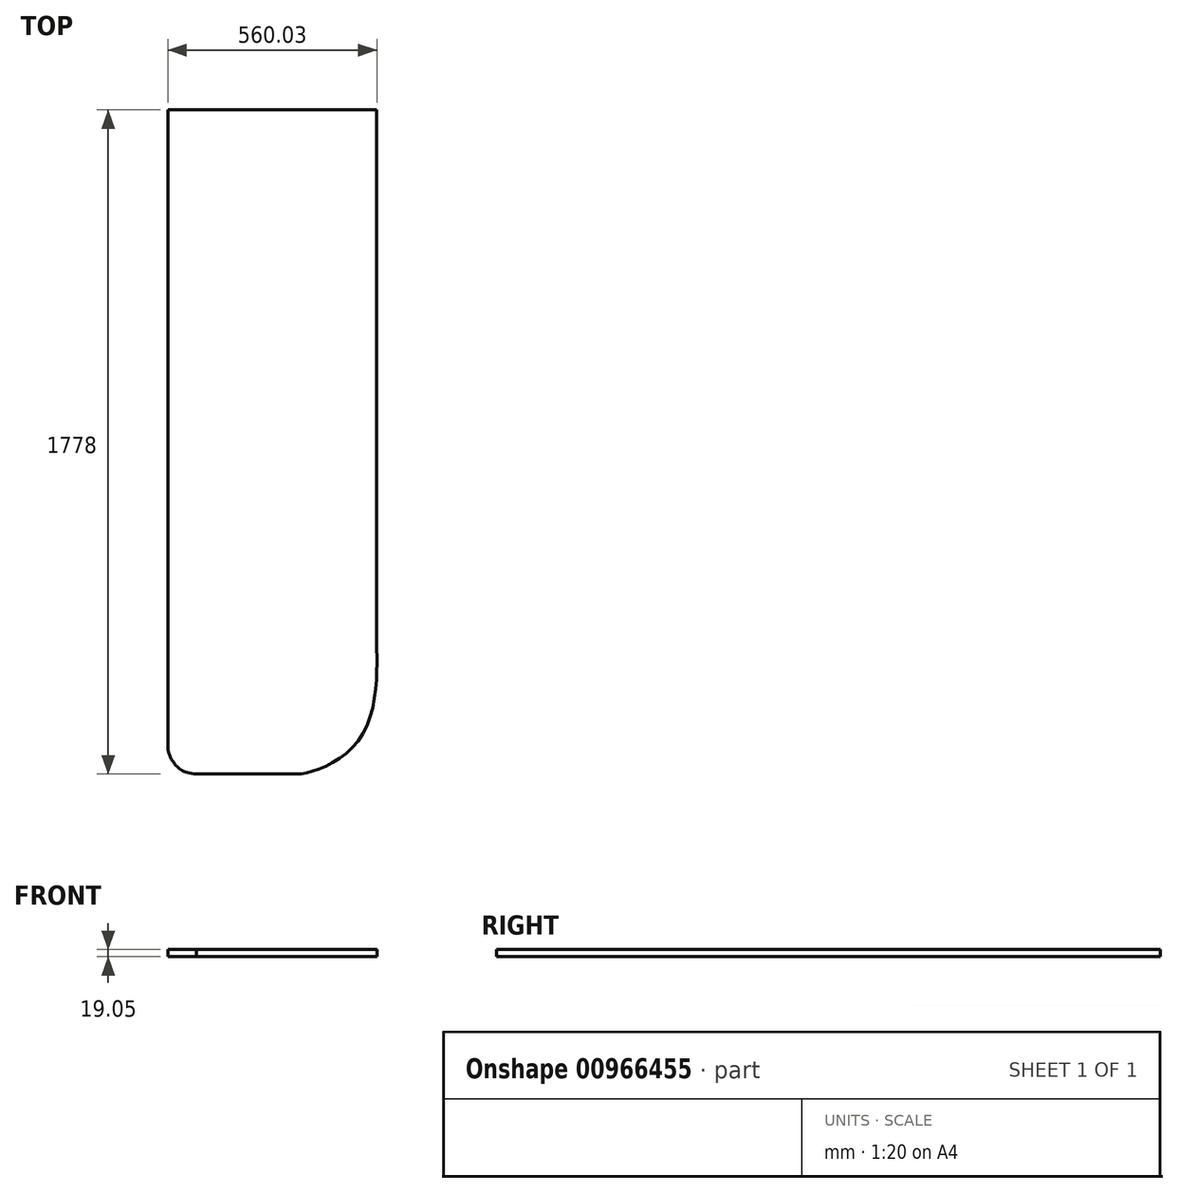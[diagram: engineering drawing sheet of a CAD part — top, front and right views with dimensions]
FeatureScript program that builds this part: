
annotation { "Feature Type Name" : "Feature", "Feature Type Description" : "" }
export const myFeature = defineFeature(function(context is Context, id is Id, definition is map)
    precondition{}
    {
        {
            var Q0;
            Q0=qCreatedBy(makeId("Top.planeOp"),FACE);
            var sketch = newSketch(context, id + "F0", { "sketchPlane" : qUnion([Q0])});
            skLineSegment(sketch, "E0.bottom", {"start": v(0, 0) * mm, "end": v(558.8, 0) * mm});
            skLineSegment(sketch, "E0.top", {"start": v(76.2, -1778) * mm, "end": v(345.36, -1778) * mm});
            skLineSegment(sketch, "E0.left", {"start": v(0, 0) * mm, "end": v(0, -1701.8) * mm});
            skLineSegment(sketch, "E0.right", {"start": v(558.8, 0) * mm, "end": v(558.8, -1422.4) * mm});
            skFitSpline(sketch, "E1", {"points": [v(345.36, -1778) * mm, v(521.71, -1671.55) * mm, v(558.8, -1422.4) * mm], "startDerivative": vector(240.18, 1.66) * mm, "endDerivative": vector(0.5, 175.33) * mm});
            skFitSpline(sketch, "E2", {"points": [v(0, -1701.8) * mm, v(22.88, -1756.18) * mm, v(76.2, -1778) * mm], "startDerivative": vector(0, -126.52) * mm, "endDerivative": vector(157.39, -10.18) * mm});
            skSolve(sketch);
        }
        {
            var Q0;
            Q0=makeQuery(id+"F0.imprint","IMPRINT",FACE,{"disambiguationData":[TD([[makeQuery(id+"F0.imprint","IMPRINT",EDGE,{"derivedFrom":sQuery(id+"F0.wireOp",EDGE,"E0.bottom")}),-1.0]])]});
            extrude(context, id + "F1", {"entities" : qUnion([Q0]), "depth" : 19.05 * mm, "offsetDistance" : 25.4 * mm});
        }
    });
